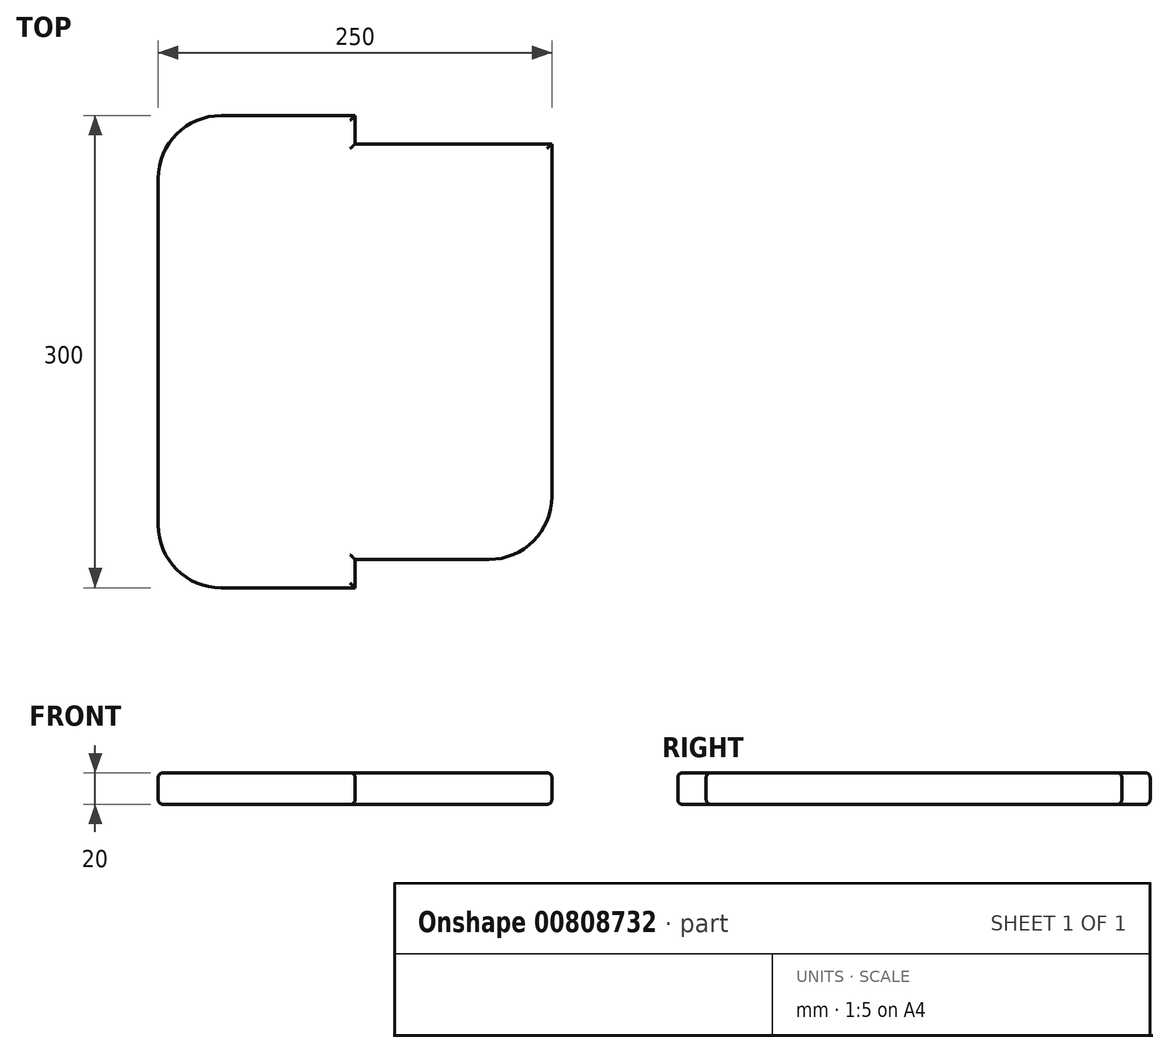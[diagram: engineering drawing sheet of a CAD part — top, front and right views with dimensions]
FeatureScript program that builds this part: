
annotation { "Feature Type Name" : "Feature", "Feature Type Description" : "" }
export const myFeature = defineFeature(function(context is Context, id is Id, definition is map)
    precondition{}
    {
        {
            var Q0;
            Q0=qCreatedBy(makeId("Front.planeOp"),FACE);
            var sketch = newSketch(context, id + "F0", { "sketchPlane" : qUnion([Q0])});
            skLineSegment(sketch, "E0", {"start": v(155.9, 0) * mm, "end": v(5, 0) * mm});
            skLineSegment(sketch, "E1", {"start": v(219.92, 144.11) * mm, "end": v(204.04, -19.68) * mm});
            skLineSegment(sketch, "E2", {"start": v(175.01, -44) * mm, "end": v(9.2, -30.74) * mm});
            skLineSegment(sketch, "E3", {"start": v(0, -5) * mm, "end": v(0, -20.77) * mm});
            skLineSegment(sketch, "E4", {"start": v(210.94, 155.03) * mm, "end": v(195.54, 156.53) * mm});
            skPoint(sketch, "E5.end.orphan", {"position": v(201.47, 150.71) * mm});
            skLineSegment(sketch, "E6", {"start": v(160.8, 4.03) * mm, "end": v(190.15, 152.52) * mm});
            skLineSegment(sketch, "E7", {"start": v(160, 0) * mm, "end": v(-37.49, 219.56) * mm, "construction": true});
            skLineSegment(sketch, "E8", {"start": v(160, 0) * mm, "end": v(235.36, -83.79) * mm, "construction": true});
            skPoint(sketch, "E9.visualSharp", {"position": v(201.47, -46.1) * mm});
            skArc(sketch, "E9.filletArc", {"start": v(175.01, -44) * mm, "mid": v(194.5, -37.78) * mm, "end": v(204.04, -19.68) * mm});
            skPoint(sketch, "E10.visualSharp", {"position": v(160, 0) * mm});
            skArc(sketch, "E10.filletArc", {"start": v(155.9, 0) * mm, "mid": v(159.07, 1.14) * mm, "end": v(160.8, 4.03) * mm});
            skPoint(sketch, "E11.visualSharp", {"position": v(220.89, 154.07) * mm});
            skArc(sketch, "E11.filletArc", {"start": v(219.92, 144.11) * mm, "mid": v(217.7, 151.43) * mm, "end": v(210.94, 155.03) * mm});
            skPoint(sketch, "E12.visualSharp", {"position": v(0, -30) * mm});
            skArc(sketch, "E12.filletArc", {"start": v(0, -20.77) * mm, "mid": v(2.65, -27.55) * mm, "end": v(9.2, -30.74) * mm});
            skPoint(sketch, "E13.visualSharp", {"position": v(191.03, 156.96) * mm});
            skArc(sketch, "E13.filletArc", {"start": v(195.54, 156.53) * mm, "mid": v(192.07, 155.56) * mm, "end": v(190.15, 152.52) * mm});
            skPoint(sketch, "E14.visualSharp", {"position": v(0, 0) * mm});
            skArc(sketch, "E14.filletArc", {"start": v(5, 0) * mm, "mid": v(1.46, -1.46) * mm, "end": v(0, -5) * mm});
            skLineSegment(sketch, "E15.bottom", {"start": v(0, -5) * mm, "end": v(45.1, -5) * mm});
            skLineSegment(sketch, "E15.top", {"start": v(0, 7.65) * mm, "end": v(45.1, 7.65) * mm});
            skLineSegment(sketch, "E15.left", {"start": v(0, -5) * mm, "end": v(0, 7.65) * mm});
            skLineSegment(sketch, "E15.right", {"start": v(45.1, -5) * mm, "end": v(45.1, 7.65) * mm});
            skSolve(sketch);
        }
        {
            var Q0;
            Q0=qCreatedBy(makeId("Top.planeOp"),FACE);
            var sketch = newSketch(context, id + "F1", { "sketchPlane" : qUnion([Q0])});
            skLineSegment(sketch, "E16.bottom", {"start": v(-125, 0) * mm, "end": v(125, 0) * mm});
            skLineSegment(sketch, "E16.top", {"start": v(-125, 300) * mm, "end": v(125, 300) * mm});
            skLineSegment(sketch, "E16.left", {"start": v(-125, 0) * mm, "end": v(-125, 300) * mm});
            skLineSegment(sketch, "E16.right", {"start": v(125, 0) * mm, "end": v(125, 300) * mm});
            skPoint(sketch, "E17", {"position": v(0, 0) * mm});
            skLineSegment(sketch, "E18", {"start": v(0, 0) * mm, "end": v(0, -165.67) * mm, "construction": true});
            skSolve(sketch);
        }
        {
            var Q0;
            Q0 = qSketchRegion(id + "F1", true);
            extrude(context, id + "F2", {"entities" : qUnion([Q0]), "oppositeDirection" : true, "depth" : 20 * mm, "offsetDistance" : 25 * mm});
        }
        {
            var Q0;
            Q0 = qSketchRegion(id + "F0", true);
            extrude(context, id + "F3", {"entities" : qUnion([Q0]), "operationType" : NewBodyOperationType.REMOVE, "oppositeDirection" : true, "depth" : 18 * mm, "offsetDistance" : 25 * mm});
        }
        {
            var Q0;
            Q0=makeQuery(id+"F2.opExtrude","SWEPT_FACE",FACE,{"disambiguationData":[OSD([sQuery(id+"F1.wireOp",EDGE,"E16.top")])]});
            var sketch = newSketch(context, id + "F4", { "sketchPlane" : qUnion([Q0])});
            skLineSegment(sketch, "E19.0", {"start": v(0, 0) * mm, "end": v(0, -20) * mm});
            skLineSegment(sketch, "E20", {"start": v(0, -20) * mm, "end": v(-125, -20) * mm});
            skLineSegment(sketch, "E21", {"start": v(-125, -20) * mm, "end": v(-125, 0) * mm});
            skLineSegment(sketch, "E22", {"start": v(-125, 0) * mm, "end": v(0, 0) * mm});
            skSolve(sketch);
        }
        {
            var Q0;
            Q0=makeQuery(id+"F4.imprint","IMPRINT",FACE,{"disambiguationData":[TD([[makeQuery(id+"F4.imprint","IMPRINT",EDGE,{"derivedFrom":sQuery(id+"F4.wireOp",EDGE,"E19.0")}),-1.0]])]});
            extrude(context, id + "F5", {"entities" : qUnion([Q0]), "operationType" : NewBodyOperationType.REMOVE, "oppositeDirection" : true, "depth" : 18 * mm, "offsetDistance" : 25 * mm});
        }
        {
            var Q0;
            Q0=makeQuery(id+"F2.opExtrude","SWEPT_EDGE",EDGE,{"disambiguationData":[OSD([sQuery(id+"F1.wireOp",EDGE,"E16.top"),sQuery(id+"F1.wireOp",EDGE,"E16.left")])]});
            var Q1;
            Q1=makeQuery(id+"F2.opExtrude","SWEPT_EDGE",EDGE,{"disambiguationData":[OSD([sQuery(id+"F1.wireOp",EDGE,"E16.bottom"),sQuery(id+"F1.wireOp",EDGE,"E16.left")])]});
            var Q2;
            Q2=makeQuery(id+"F5.boolean.opBoolean","COPY",EDGE,{"derivedFrom":makeQuery(id+"F5.opExtrude","CAP_EDGE",EDGE,{"disambiguationData":[OSD([sQuery(id+"F4.wireOp",EDGE,"E21")])],"isStart":false})});
            var Q3;
            Q3=makeQuery(id+"F3.boolean.opBoolean","INTERSECT",EDGE,{"derivedFrom":[makeQuery(id+"F2.opExtrude","SWEPT_FACE",FACE,{"disambiguationData":[OSD([sQuery(id+"F1.wireOp",EDGE,"E16.right")])]}),makeQuery(id+"F3.opExtrude","CAP_FACE",FACE,{"disambiguationData":[OSD([sQuery(id+"F0.wireOp",EDGE,"E0"),sQuery(id+"F0.wireOp",EDGE,"E1"),sQuery(id+"F0.wireOp",EDGE,"E2"),sQuery(id+"F0.wireOp",EDGE,"E3"),sQuery(id+"F0.wireOp",EDGE,"E4"),sQuery(id+"F0.wireOp",EDGE,"E6"),sQuery(id+"F0.wireOp",EDGE,"E9.filletArc"),sQuery(id+"F0.wireOp",EDGE,"E10.filletArc"),sQuery(id+"F0.wireOp",EDGE,"E11.filletArc"),sQuery(id+"F0.wireOp",EDGE,"E12.filletArc"),sQuery(id+"F0.wireOp",EDGE,"E13.filletArc"),sQuery(id+"F0.wireOp",EDGE,"E15.top"),sQuery(id+"F0.wireOp",EDGE,"E15.left"),sQuery(id+"F0.wireOp",EDGE,"E15.right")])],"isStart":false})]});
            fillet(context, id + "F6", {"entities" : qUnion([Q0, Q1, Q2, Q3]), "radius" : 40 * mm, "tangentPropagation" : true, "allowEdgeOverflow" : false});
        }
        {
            var Q0;
            Q0=makeQuery(id+"F3.boolean.opBoolean","COPY",EDGE,{"derivedFrom":makeQuery(id+"F3.opExtrude","CAP_EDGE",EDGE,{"disambiguationData":[OSD([sQuery(id+"F0.wireOp",EDGE,"E3"),sQuery(id+"F0.wireOp",EDGE,"E15.left")])],"isStart":true})});
            var Q1;
            Q1=makeQuery(id+"F5.boolean.opBoolean","COPY",EDGE,{"derivedFrom":makeQuery(id+"F5.opExtrude","CAP_EDGE",EDGE,{"disambiguationData":[OSD([sQuery(id+"F4.wireOp",EDGE,"E19.0")])],"isStart":true})});
            var Q2;
            Q2=makeQuery(id+"F2.opExtrude","CAP_FACE",FACE,{"disambiguationData":[OSD([sQuery(id+"F1.wireOp",EDGE,"E16.bottom"),sQuery(id+"F1.wireOp",EDGE,"E16.top"),sQuery(id+"F1.wireOp",EDGE,"E16.left"),sQuery(id+"F1.wireOp",EDGE,"E16.right")])],"isStart":true});
            var Q3;
            Q3=makeQuery(id+"F2.opExtrude","CAP_FACE",FACE,{"disambiguationData":[OSD([sQuery(id+"F1.wireOp",EDGE,"E16.bottom"),sQuery(id+"F1.wireOp",EDGE,"E16.top"),sQuery(id+"F1.wireOp",EDGE,"E16.left"),sQuery(id+"F1.wireOp",EDGE,"E16.right")])],"isStart":false});
            fillet(context, id + "F7", {"entities" : qUnion([Q0, Q1, Q2, Q3]), "radius" : 3 * mm, "tangentPropagation" : true, "allowEdgeOverflow" : false});
        }
        {
            var Q0;
            Q0=makeQuery(id+"F3.boolean.opBoolean","COPY",FACE,{"derivedFrom":makeQuery(id+"F3.opExtrude","CAP_FACE",FACE,{"disambiguationData":[OSD([sQuery(id+"F0.wireOp",EDGE,"E0"),sQuery(id+"F0.wireOp",EDGE,"E1"),sQuery(id+"F0.wireOp",EDGE,"E2"),sQuery(id+"F0.wireOp",EDGE,"E3"),sQuery(id+"F0.wireOp",EDGE,"E4"),sQuery(id+"F0.wireOp",EDGE,"E6"),sQuery(id+"F0.wireOp",EDGE,"E9.filletArc"),sQuery(id+"F0.wireOp",EDGE,"E10.filletArc"),sQuery(id+"F0.wireOp",EDGE,"E11.filletArc"),sQuery(id+"F0.wireOp",EDGE,"E12.filletArc"),sQuery(id+"F0.wireOp",EDGE,"E13.filletArc"),sQuery(id+"F0.wireOp",EDGE,"E15.top"),sQuery(id+"F0.wireOp",EDGE,"E15.left"),sQuery(id+"F0.wireOp",EDGE,"E15.right")])],"isStart":false})});
            var sketch = newSketch(context, id + "F8", { "sketchPlane" : qUnion([Q0])});
            skPoint(sketch, "E23.0", {"position": v(0, -10) * mm});
            skLineSegment(sketch, "E24", {"start": v(0, -10) * mm, "end": v(50, -10) * mm, "construction": true});
            skPoint(sketch, "E25", {"position": v(50, -10) * mm});
            skSolve(sketch);
        }
        {
            var Q0;
            Q0=makeQuery(id+"F5.boolean.opBoolean","COPY",FACE,{"derivedFrom":makeQuery(id+"F5.opExtrude","CAP_FACE",FACE,{"disambiguationData":[OSD([sQuery(id+"F4.wireOp",EDGE,"E19.0"),sQuery(id+"F4.wireOp",EDGE,"E20"),sQuery(id+"F4.wireOp",EDGE,"E21"),sQuery(id+"F4.wireOp",EDGE,"E22")])],"isStart":false})});
            var sketch = newSketch(context, id + "F9", { "sketchPlane" : qUnion([Q0])});
            skPoint(sketch, "E26.0", {"position": v(-50, -10) * mm});
            skSolve(sketch);
        }
    });
